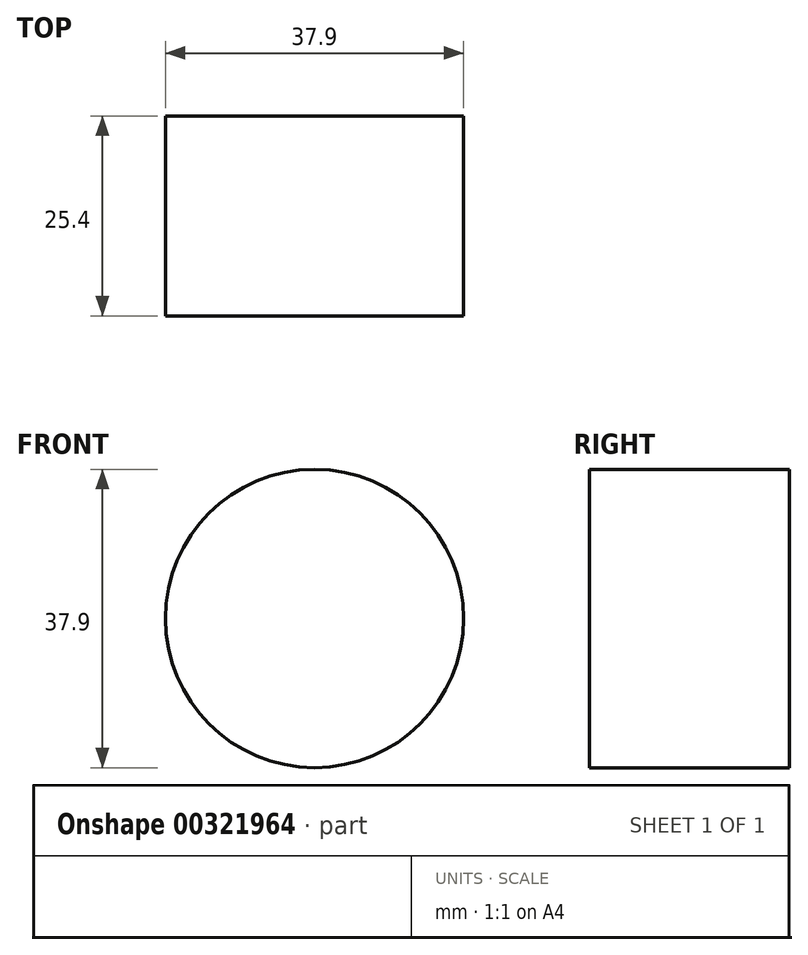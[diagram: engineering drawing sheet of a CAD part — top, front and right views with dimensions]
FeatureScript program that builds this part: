
annotation { "Feature Type Name" : "Feature", "Feature Type Description" : "" }
export const myFeature = defineFeature(function(context is Context, id is Id, definition is map)
    precondition{}
    {
        {
            var Q0;
            Q0=qCreatedBy(makeId("Front.planeOp"),FACE);
            var sketch = newSketch(context, id + "F0", { "sketchPlane" : qUnion([Q0])});
            skCircle(sketch, "E0", {"center": v(0, 0) * mm, "radius": 18.95 * mm});
            skSolve(sketch);
        }
        {
            var Q0;
            Q0 = qSketchRegion(id + "F0", true);
            extrude(context, id + "F1", {"entities" : qUnion([Q0]), "depth" : 25.4 * mm});
        }
    });
